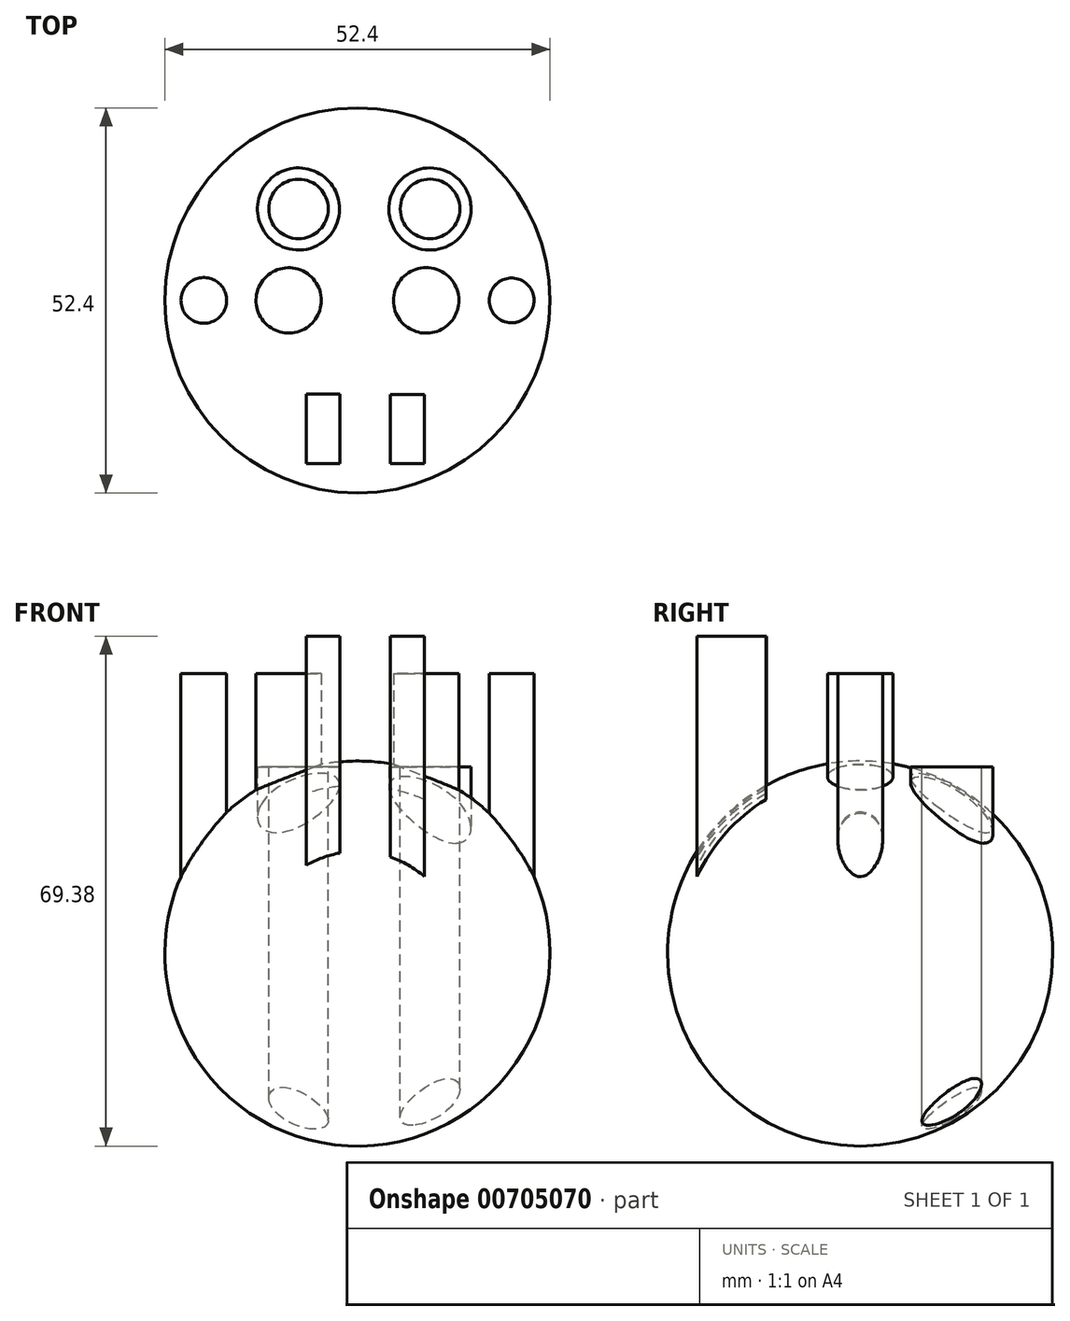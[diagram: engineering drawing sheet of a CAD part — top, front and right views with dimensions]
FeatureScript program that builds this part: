
annotation { "Feature Type Name" : "Feature", "Feature Type Description" : "" }
export const myFeature = defineFeature(function(context is Context, id is Id, definition is map)
    precondition{}
    {
        {
            var Q0;
            Q0=qCreatedBy(makeId("Top.planeOp"),FACE);
            var sketch = newSketch(context, id + "F0", { "sketchPlane" : qUnion([Q0])});
            skCircle(sketch, "E0", {"center": v(0, 0) * mm, "radius": 26.2 * mm});
            skLineSegment(sketch, "E1", {"start": v(0, 0) * mm, "end": v(0, 76.59) * mm});
            skLineSegment(sketch, "E2", {"start": v(0, 0) * mm, "end": v(0, -67.45) * mm});
            skSolve(sketch);
        }
        {
            var Q0;
            {var subQ0=sQuery(id+"F0.wireOp",EDGE,"E1");var subQ1=sQuery(id+"F0.wireOp",EDGE,"E0");var subQ2=makeQuery(id+"F0.imprint","INTERSECT",VERTEX,{"derivedFrom":[subQ1,subQ0]});Q0=makeQuery(id+"F0.imprint","IMPRINT",FACE,{"disambiguationData":[TD([[makeQuery(id+"F0.imprint","IMPRINT",EDGE,{"disambiguationData":[TD([[subQ2,-1.0]])],"derivedFrom":subQ1}),1.0]])]});}
            var Q1;
            Q1=sQuery(id+"F0.wireOp",EDGE,"E2");
            revolve(context, id + "F1", {"surfaceOperationType" : NewSurfaceOperationType.NEW, "entities" : qUnion([Q0]), "axis" : qUnion([Q1]), "revolveType" : RevolveType.FULL});
        }
        {
            var Q0;
            Q0=qCreatedBy(makeId("Top.planeOp"),FACE);
            var sketch = newSketch(context, id + "F2", { "sketchPlane" : qUnion([Q0])});
            skCircle(sketch, "E3", {"center": v(-8.02, 12.44) * mm, "radius": 5.59 * mm});
            skCircle(sketch, "E4", {"center": v(9.86, 12.44) * mm, "radius": 5.59 * mm});
            skSolve(sketch);
        }
        {
            var Q0;
            Q0 = qSketchRegion(id + "F2", true);
            extrude(context, id + "F3", {"entities" : qUnion([Q0]), "operationType" : NewBodyOperationType.ADD, "depth" : 25.4 * mm, "offsetDistance" : 25.4 * mm});
        }
        {
            var Q0;
            Q0=qCreatedBy(makeId("Top.planeOp"),FACE);
            var sketch = newSketch(context, id + "F4", { "sketchPlane" : qUnion([Q0])});
            skCircle(sketch, "E5", {"center": v(-20.9, 0) * mm, "radius": 3.11 * mm});
            skCircle(sketch, "E6", {"center": v(20.97, 0) * mm, "radius": 3.05 * mm});
            skCircle(sketch, "E7", {"center": v(-9.36, 0) * mm, "radius": 4.45 * mm});
            skCircle(sketch, "E8", {"center": v(9.35, 0) * mm, "radius": 4.46 * mm});
            skSolve(sketch);
        }
        {
            var Q0;
            Q0 = qSketchRegion(id + "F4", true);
            extrude(context, id + "F5", {"entities" : qUnion([Q0]), "operationType" : NewBodyOperationType.ADD, "depth" : 38.1 * mm, "offsetDistance" : 25.4 * mm});
        }
        {
            var Q0;
            Q0=qCreatedBy(makeId("Top.planeOp"),FACE);
            var sketch = newSketch(context, id + "F6", { "sketchPlane" : qUnion([Q0])});
            skLineSegment(sketch, "E9.bottom", {"start": v(-2.39, -12.77) * mm, "end": v(-6.96, -12.77) * mm});
            skLineSegment(sketch, "E9.top", {"start": v(-2.39, -22.22) * mm, "end": v(-6.96, -22.22) * mm});
            skLineSegment(sketch, "E9.left", {"start": v(-2.39, -12.77) * mm, "end": v(-2.39, -22.22) * mm});
            skLineSegment(sketch, "E9.right", {"start": v(-6.96, -12.77) * mm, "end": v(-6.96, -22.22) * mm});
            skLineSegment(sketch, "E10.bottom", {"start": v(4.47, -22.22) * mm, "end": v(9.09, -22.22) * mm});
            skLineSegment(sketch, "E10.top", {"start": v(4.47, -12.82) * mm, "end": v(9.09, -12.82) * mm});
            skLineSegment(sketch, "E10.left", {"start": v(4.47, -22.22) * mm, "end": v(4.47, -12.82) * mm});
            skLineSegment(sketch, "E10.right", {"start": v(9.09, -22.22) * mm, "end": v(9.09, -12.82) * mm});
            skSolve(sketch);
        }
        {
            var Q0;
            Q0 = qSketchRegion(id + "F6", true);
            extrude(context, id + "F7", {"entities" : qUnion([Q0]), "operationType" : NewBodyOperationType.ADD, "depth" : 43.18 * mm, "offsetDistance" : 25.4 * mm});
        }
        {
            var Q0;
            Q0=qCreatedBy(makeId("Top.planeOp"),FACE);
            var sketch = newSketch(context, id + "F8", { "sketchPlane" : qUnion([Q0])});
            skCircle(sketch, "E11", {"center": v(-7.21, 12.67) * mm, "radius": 2.92 * mm});
            skCircle(sketch, "E12", {"center": v(9.1, 12.67) * mm, "radius": 2.92 * mm});
            skSolve(sketch);
        }
        {
            var Q0;
            Q0 = qSketchRegion(id + "F8", true);
            extrude(context, id + "F9", {"entities" : qUnion([Q0]), "operationType" : NewBodyOperationType.REMOVE, "oppositeDirection" : true, "depth" : 7620 * mm, "offsetDistance" : 25.4 * mm});
        }
        {
            var Q0;
            Q0=makeQuery(id+"F3.opExtrude","CAP_FACE",FACE,{"disambiguationData":[OSD([sQuery(id+"F2.wireOp",EDGE,"E3")])],"isStart":false});
            var sketch = newSketch(context, id + "F10", { "sketchPlane" : qUnion([Q0])});
            skCircle(sketch, "E13", {"center": v(-8.02, 12.44) * mm, "radius": 4.05 * mm});
            skCircle(sketch, "E14", {"center": v(9.87, 12.46) * mm, "radius": 4.05 * mm});
            skSolve(sketch);
        }
        {
            var Q0;
            Q0 = qSketchRegion(id + "F10", true);
            extrude(context, id + "F11", {"entities" : qUnion([Q0]), "operationType" : NewBodyOperationType.REMOVE, "oppositeDirection" : true, "depth" : 7620 * mm, "offsetDistance" : 25.4 * mm});
        }
    });
